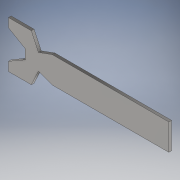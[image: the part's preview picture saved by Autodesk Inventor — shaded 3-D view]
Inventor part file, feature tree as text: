
AUTODESK INVENTOR PART (.ipt)
format: ipt  version: 2021 (Build 250183000, 183)  size: 134,656 bytes
history: native  units: mm
features: extrude x1, sketch x1
ambient origin geometry x8: Origin, YZ Plane, XZ Plane, XY Plane, X Axis, Y Axis, Z Axis, Center Point
bodies: Solid1 (feature_tree)
feature tree (2):
  extrude  "Extrusion1"  Depth=18.0mm
  sketch  "Sketch1"  dims[d0=80.0mm d1=18.0mm d2=30.0mm d3=0.0mm d4=7.0mm d5=7.0mm d6=27.925268mm d7=27.925268mm d8=10.0mm d9=10.0mm d10=20.071286mm d11=20.071286mm d12=6.0mm d13=120.0deg d14=6.0mm d15=120.0deg d16=30.0mm d17=1.905mm d18=0.0mm]
